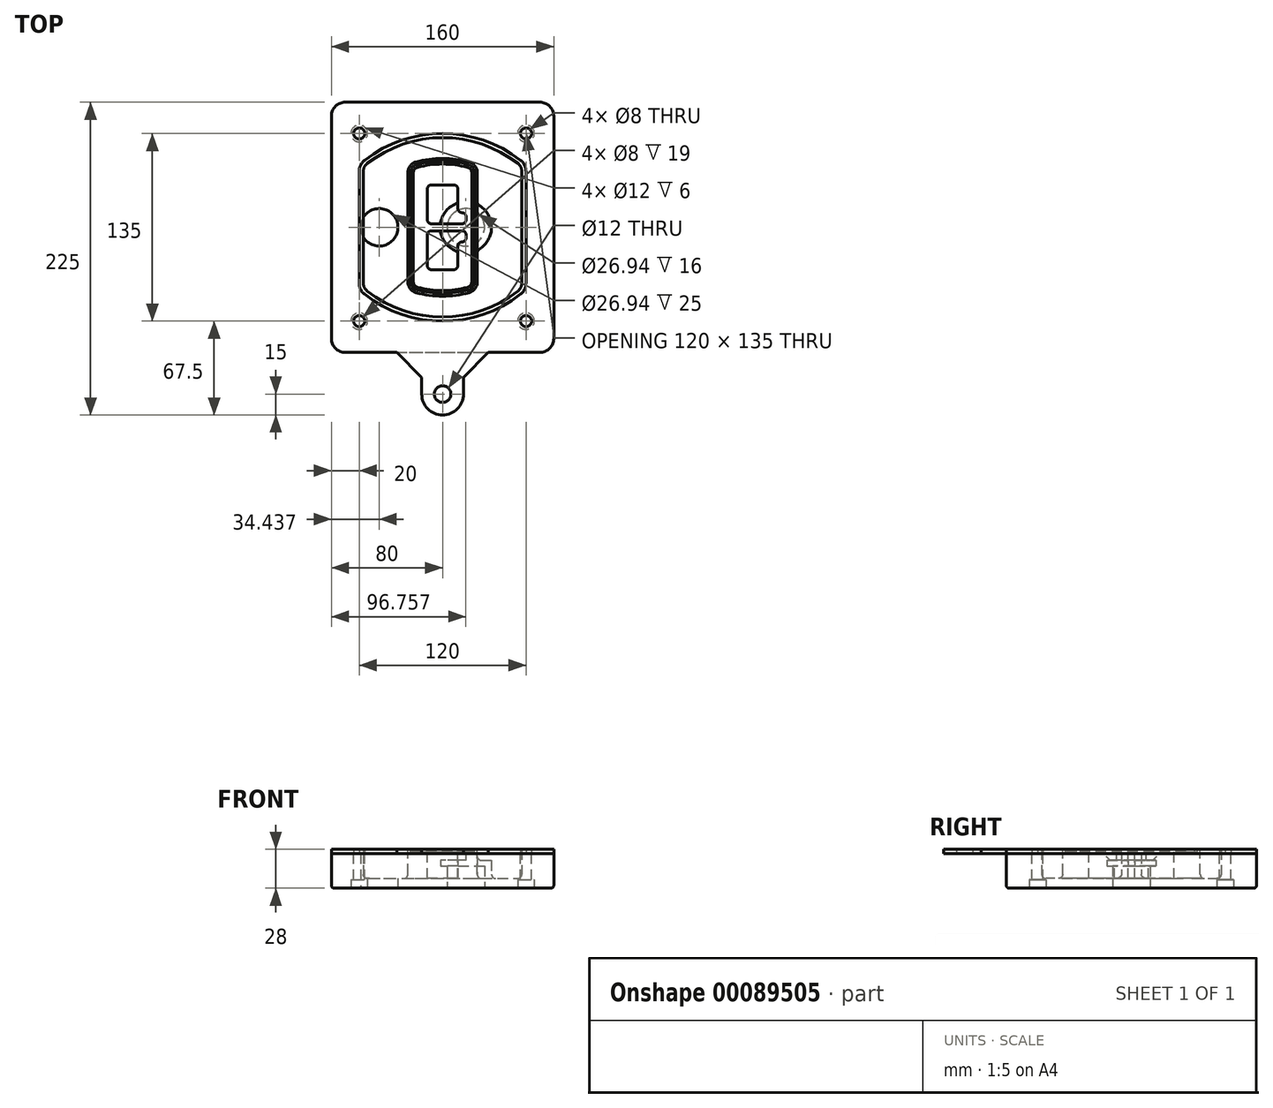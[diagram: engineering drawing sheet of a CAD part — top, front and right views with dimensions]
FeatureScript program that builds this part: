
annotation { "Feature Type Name" : "Feature", "Feature Type Description" : "" }
export const myFeature = defineFeature(function(context is Context, id is Id, definition is map)
    precondition{}
    {
        {
            var Q0;
            Q0=qCreatedBy(makeId("Top.planeOp"),FACE);
            var sketch = newSketch(context, id + "F0", { "sketchPlane" : qUnion([Q0])});
            skPoint(sketch, "E0.rect.middle", {"position": v(0, 0) * mm});
            skLineSegment(sketch, "E1.bottom", {"start": v(-70, -90) * mm, "end": v(70, -90) * mm});
            skLineSegment(sketch, "E1.top", {"start": v(-70, 90) * mm, "end": v(70, 90) * mm});
            skLineSegment(sketch, "E1.left", {"start": v(-80, -80) * mm, "end": v(-80, 80) * mm});
            skLineSegment(sketch, "E1.right", {"start": v(80, -80) * mm, "end": v(80, 80) * mm});
            skLineSegment(sketch, "E2", {"start": v(-80, 90) * mm, "end": v(80, -90) * mm, "construction": true});
            skLineSegment(sketch, "E3", {"start": v(80, 90) * mm, "end": v(-80, -90) * mm, "construction": true});
            skCircle(sketch, "E4", {"center": v(-60, 67.5) * mm, "radius": 4 * mm});
            skCircle(sketch, "E5", {"center": v(60, 67.5) * mm, "radius": 4 * mm});
            skCircle(sketch, "E6", {"center": v(60, -67.5) * mm, "radius": 4 * mm});
            skCircle(sketch, "E7", {"center": v(-60, -67.5) * mm, "radius": 4 * mm});
            skLineSegment(sketch, "E8", {"start": v(-60, 67.5) * mm, "end": v(60, 67.5) * mm, "construction": true});
            skLineSegment(sketch, "E9", {"start": v(60, 67.5) * mm, "end": v(60, -67.5) * mm, "construction": true});
            skLineSegment(sketch, "E10", {"start": v(60, -67.5) * mm, "end": v(-60, -67.5) * mm, "construction": true});
            skLineSegment(sketch, "E11", {"start": v(-60, -67.5) * mm, "end": v(-60, 67.5) * mm, "construction": true});
            skLineSegment(sketch, "E12", {"start": v(-60, 40.3) * mm, "end": v(-60, -40.3) * mm});
            skLineSegment(sketch, "E13", {"start": v(60, 40.3) * mm, "end": v(60, -40.3) * mm});
            skArc(sketch, "E14", {"start": v(56.15, 48.18) * mm, "mid": v(0, 67.5) * mm, "end": v(-56.15, 48.18) * mm});
            skArc(sketch, "E15", {"start": v(-56.15, -48.18) * mm, "mid": v(0, -67.5) * mm, "end": v(56.15, -48.18) * mm});
            skLineSegment(sketch, "E16", {"start": v(-60, 0) * mm, "end": v(60, 0) * mm, "construction": true});
            skPoint(sketch, "E17.visualSharp", {"position": v(-60, -45) * mm});
            skArc(sketch, "E17.filletArc", {"start": v(-60, -40.3) * mm, "mid": v(-58.99, -44.68) * mm, "end": v(-56.15, -48.18) * mm});
            skPoint(sketch, "E18.visualSharp", {"position": v(-60, 45) * mm});
            skArc(sketch, "E18.filletArc", {"start": v(-56.15, 48.18) * mm, "mid": v(-58.99, 44.68) * mm, "end": v(-60, 40.3) * mm});
            skPoint(sketch, "E19.visualSharp", {"position": v(60, 45) * mm});
            skArc(sketch, "E19.filletArc", {"start": v(60, 40.3) * mm, "mid": v(58.99, 44.68) * mm, "end": v(56.15, 48.18) * mm});
            skPoint(sketch, "E20.visualSharp", {"position": v(60, -45) * mm});
            skArc(sketch, "E20.filletArc", {"start": v(56.15, -48.18) * mm, "mid": v(58.99, -44.68) * mm, "end": v(60, -40.3) * mm});
            skPoint(sketch, "E21.visualSharp", {"position": v(-80, 90) * mm});
            skArc(sketch, "E21.filletArc", {"start": v(-70, 90) * mm, "mid": v(-77.07, 87.07) * mm, "end": v(-80, 80) * mm});
            skPoint(sketch, "E22.visualSharp", {"position": v(80, 90) * mm});
            skArc(sketch, "E22.filletArc", {"start": v(80, 80) * mm, "mid": v(77.07, 87.07) * mm, "end": v(70, 90) * mm});
            skPoint(sketch, "E23.visualSharp", {"position": v(80, -90) * mm});
            skArc(sketch, "E23.filletArc", {"start": v(70, -90) * mm, "mid": v(77.07, -87.07) * mm, "end": v(80, -80) * mm});
            skPoint(sketch, "E24.visualSharp", {"position": v(-80, -90) * mm});
            skArc(sketch, "E24.filletArc", {"start": v(-80, -80) * mm, "mid": v(-77.07, -87.07) * mm, "end": v(-70, -90) * mm});
            skArc(sketch, "E25.0", {"start": v(57, 40.3) * mm, "mid": v(56.3, 43.36) * mm, "end": v(54.3, 45.81) * mm});
            skLineSegment(sketch, "E25.1", {"start": v(57, 40.3) * mm, "end": v(57, -40.3) * mm});
            skArc(sketch, "E25.2", {"start": v(54.3, -45.81) * mm, "mid": v(56.3, -43.36) * mm, "end": v(57, -40.3) * mm});
            skArc(sketch, "E25.3", {"start": v(-54.3, -45.81) * mm, "mid": v(0, -64.5) * mm, "end": v(54.3, -45.81) * mm});
            skArc(sketch, "E25.4", {"start": v(-57, -40.3) * mm, "mid": v(-56.3, -43.36) * mm, "end": v(-54.3, -45.81) * mm});
            skArc(sketch, "E25.5", {"start": v(54.3, 45.81) * mm, "mid": v(0, 64.5) * mm, "end": v(-54.3, 45.81) * mm});
            skLineSegment(sketch, "E25.6", {"start": v(-57, 40.3) * mm, "end": v(-57, -40.3) * mm});
            skArc(sketch, "E25.7", {"start": v(-54.3, 45.81) * mm, "mid": v(-56.3, 43.36) * mm, "end": v(-57, 40.3) * mm});
            skArc(sketch, "E26.0", {"start": v(-58.62, 51.33) * mm, "mid": v(-62.58, 46.43) * mm, "end": v(-64, 40.3) * mm});
            skArc(sketch, "E26.1", {"start": v(58.62, 51.33) * mm, "mid": v(0, 71.5) * mm, "end": v(-58.62, 51.33) * mm});
            skArc(sketch, "E26.2", {"start": v(64, 40.3) * mm, "mid": v(62.58, 46.43) * mm, "end": v(58.62, 51.33) * mm});
            skLineSegment(sketch, "E26.3", {"start": v(64, 40.3) * mm, "end": v(64, -40.3) * mm});
            skArc(sketch, "E26.4", {"start": v(58.62, -51.33) * mm, "mid": v(62.58, -46.43) * mm, "end": v(64, -40.3) * mm});
            skLineSegment(sketch, "E26.5", {"start": v(-64, 40.3) * mm, "end": v(-64, -40.3) * mm});
            skArc(sketch, "E26.6", {"start": v(-58.62, -51.33) * mm, "mid": v(0, -71.5) * mm, "end": v(58.62, -51.33) * mm});
            skArc(sketch, "E26.7", {"start": v(-64, -40.3) * mm, "mid": v(-62.58, -46.43) * mm, "end": v(-58.62, -51.33) * mm});
            skSolve(sketch);
        }
        {
            var Q0;
            Q0=makeQuery(id+"F0.imprint","IMPRINT",FACE,{"disambiguationData":[TD([[makeQuery(id+"F0.imprint","IMPRINT",EDGE,{"derivedFrom":sQuery(id+"F0.wireOp",EDGE,"E1.bottom")}),1.0]])]});
            var Q1;
            Q1=makeQuery(id+"F0.imprint","IMPRINT",FACE,{"disambiguationData":[TD([[makeQuery(id+"F0.imprint","IMPRINT",EDGE,{"derivedFrom":sQuery(id+"F0.wireOp",EDGE,"E12")}),1.0]])]});
            var Q2;
            Q2=makeQuery(id+"F0.imprint","IMPRINT",FACE,{"disambiguationData":[TD([[makeQuery(id+"F0.imprint","IMPRINT",EDGE,{"derivedFrom":sQuery(id+"F0.wireOp",EDGE,"E25.0")}),1.0]])]});
            var Q3;
            Q3=makeQuery(id+"F0.imprint","IMPRINT",FACE,{"disambiguationData":[TD([[makeQuery(id+"F0.imprint","IMPRINT",EDGE,{"derivedFrom":sQuery(id+"F0.wireOp",EDGE,"E12")}),-1.0]])]});
            extrude(context, id + "F1", {"entities" : qUnion([Q0, Q1, Q2, Q3]), "oppositeDirection" : true, "depth" : 25 * mm});
        }
        {
            var Q0;
            Q0=makeQuery(id+"F0.imprint","IMPRINT",FACE,{"disambiguationData":[TD([[makeQuery(id+"F0.imprint","IMPRINT",EDGE,{"derivedFrom":sQuery(id+"F0.wireOp",EDGE,"E12")}),1.0]])]});
            extrude(context, id + "F2", {"entities" : qUnion([Q0]), "operationType" : NewBodyOperationType.ADD, "depth" : 3 * mm});
        }
        {
            var Q0;
            Q0=makeQuery(id+"F0.imprint","IMPRINT",FACE,{"disambiguationData":[TD([[makeQuery(id+"F0.imprint","IMPRINT",EDGE,{"derivedFrom":sQuery(id+"F0.wireOp",EDGE,"E25.0")}),1.0]])]});
            extrude(context, id + "F3", {"entities" : qUnion([Q0]), "operationType" : NewBodyOperationType.REMOVE, "oppositeDirection" : true, "depth" : 18 * mm});
        }
        {
            var Q0;
            Q0=makeQuery(id+"F2.opExtrude","CAP_FACE",FACE,{"disambiguationData":[OSD([sQuery(id+"F0.wireOp",EDGE,"E12"),sQuery(id+"F0.wireOp",EDGE,"E13"),sQuery(id+"F0.wireOp",EDGE,"E14"),sQuery(id+"F0.wireOp",EDGE,"E15"),sQuery(id+"F0.wireOp",EDGE,"E17.filletArc"),sQuery(id+"F0.wireOp",EDGE,"E18.filletArc"),sQuery(id+"F0.wireOp",EDGE,"E19.filletArc"),sQuery(id+"F0.wireOp",EDGE,"E20.filletArc"),sQuery(id+"F0.wireOp",EDGE,"E25.0"),sQuery(id+"F0.wireOp",EDGE,"E25.1"),sQuery(id+"F0.wireOp",EDGE,"E25.2"),sQuery(id+"F0.wireOp",EDGE,"E25.3"),sQuery(id+"F0.wireOp",EDGE,"E25.4"),sQuery(id+"F0.wireOp",EDGE,"E25.5"),sQuery(id+"F0.wireOp",EDGE,"E25.6"),sQuery(id+"F0.wireOp",EDGE,"E25.7")])],"isStart":false});
            var sketch = newSketch(context, id + "F4", { "sketchPlane" : qUnion([Q0])});
            skArc(sketch, "E27.0", {"start": v(-19.08, -46.97) * mm, "mid": v(0, -49.5) * mm, "end": v(19.08, -46.97) * mm});
            skArc(sketch, "E28.0", {"start": v(19.08, 46.97) * mm, "mid": v(0, 49.5) * mm, "end": v(-19.08, 46.97) * mm});
            skLineSegment(sketch, "E29", {"start": v(-25, 39.25) * mm, "end": v(-25, -39.25) * mm});
            skLineSegment(sketch, "E30", {"start": v(25, 39.25) * mm, "end": v(25, -39.25) * mm});
            skLineSegment(sketch, "E31", {"start": v(-25, 45.1) * mm, "end": v(25, 45.1) * mm, "construction": true});
            skLineSegment(sketch, "E32", {"start": v(-25, -45.1) * mm, "end": v(25, -45.1) * mm, "construction": true});
            skPoint(sketch, "E33.visualSharp", {"position": v(-25, 45.1) * mm});
            skArc(sketch, "E33.filletArc", {"start": v(-19.08, 46.97) * mm, "mid": v(-23.35, 44.11) * mm, "end": v(-25, 39.25) * mm});
            skPoint(sketch, "E34.visualSharp", {"position": v(25, 45.1) * mm});
            skArc(sketch, "E34.filletArc", {"start": v(25, 39.25) * mm, "mid": v(23.35, 44.11) * mm, "end": v(19.08, 46.97) * mm});
            skPoint(sketch, "E35.visualSharp", {"position": v(25, -45.1) * mm});
            skArc(sketch, "E35.filletArc", {"start": v(19.08, -46.97) * mm, "mid": v(23.35, -44.11) * mm, "end": v(25, -39.25) * mm});
            skPoint(sketch, "E36.visualSharp", {"position": v(-25, -45.1) * mm});
            skArc(sketch, "E36.filletArc", {"start": v(-25, -39.25) * mm, "mid": v(-23.35, -44.11) * mm, "end": v(-19.08, -46.97) * mm});
            skArc(sketch, "E37.0", {"start": v(54.3, 45.81) * mm, "mid": v(0, 64.5) * mm, "end": v(-54.3, 45.81) * mm});
            skArc(sketch, "E37.1", {"start": v(-54.3, 45.81) * mm, "mid": v(-56.3, 43.36) * mm, "end": v(-57, 40.3) * mm});
            skLineSegment(sketch, "E37.2", {"start": v(-57, 40.3) * mm, "end": v(-57, -40.3) * mm});
            skArc(sketch, "E37.3", {"start": v(-57, -40.3) * mm, "mid": v(-56.3, -43.36) * mm, "end": v(-54.3, -45.81) * mm});
            skArc(sketch, "E37.4", {"start": v(-54.3, -45.81) * mm, "mid": v(0, -64.5) * mm, "end": v(54.3, -45.81) * mm});
            skArc(sketch, "E37.5", {"start": v(54.3, -45.81) * mm, "mid": v(56.3, -43.36) * mm, "end": v(57, -40.3) * mm});
            skLineSegment(sketch, "E37.6", {"start": v(57, 40.3) * mm, "end": v(57, -40.3) * mm});
            skArc(sketch, "E37.7", {"start": v(57, 40.3) * mm, "mid": v(56.3, 43.36) * mm, "end": v(54.3, 45.81) * mm});
            skLineSegment(sketch, "E38.0", {"start": v(23, 39.25) * mm, "end": v(23, -39.25) * mm});
            skArc(sketch, "E38.1", {"start": v(18.56, -45.04) * mm, "mid": v(21.76, -42.9) * mm, "end": v(23, -39.25) * mm});
            skArc(sketch, "E38.2", {"start": v(-18.56, -45.04) * mm, "mid": v(0, -47.5) * mm, "end": v(18.56, -45.04) * mm});
            skArc(sketch, "E38.3", {"start": v(-23, -39.25) * mm, "mid": v(-21.76, -42.9) * mm, "end": v(-18.56, -45.04) * mm});
            skLineSegment(sketch, "E38.4", {"start": v(-23, 39.25) * mm, "end": v(-23, -39.25) * mm});
            skArc(sketch, "E38.5", {"start": v(23, 39.25) * mm, "mid": v(21.76, 42.9) * mm, "end": v(18.56, 45.04) * mm});
            skArc(sketch, "E38.6", {"start": v(-18.56, 45.04) * mm, "mid": v(-21.76, 42.9) * mm, "end": v(-23, 39.25) * mm});
            skArc(sketch, "E38.7", {"start": v(18.56, 45.04) * mm, "mid": v(0, 47.5) * mm, "end": v(-18.56, 45.04) * mm});
            skArc(sketch, "E39.0", {"start": v(21, 39.25) * mm, "mid": v(20.18, 41.68) * mm, "end": v(18.04, 43.1) * mm});
            skLineSegment(sketch, "E39.1", {"start": v(21, 39.25) * mm, "end": v(21, -39.25) * mm});
            skArc(sketch, "E39.2", {"start": v(18.04, -43.1) * mm, "mid": v(20.18, -41.68) * mm, "end": v(21, -39.25) * mm});
            skArc(sketch, "E39.3", {"start": v(-18.04, -43.1) * mm, "mid": v(0, -45.5) * mm, "end": v(18.04, -43.1) * mm});
            skArc(sketch, "E39.4", {"start": v(-21, -39.25) * mm, "mid": v(-20.18, -41.68) * mm, "end": v(-18.04, -43.1) * mm});
            skArc(sketch, "E39.5", {"start": v(18.04, 43.1) * mm, "mid": v(0, 45.5) * mm, "end": v(-18.04, 43.1) * mm});
            skLineSegment(sketch, "E39.6", {"start": v(-21, 39.25) * mm, "end": v(-21, -39.25) * mm});
            skArc(sketch, "E39.7", {"start": v(-18.04, 43.1) * mm, "mid": v(-20.18, 41.68) * mm, "end": v(-21, 39.25) * mm});
            skLineSegment(sketch, "E40", {"start": v(-25, 0) * mm, "end": v(25, 0) * mm, "construction": true});
            skLineSegment(sketch, "E41", {"start": v(-11, 5.5) * mm, "end": v(-11, 27.5) * mm});
            skLineSegment(sketch, "E42", {"start": v(-8, 30.5) * mm, "end": v(8, 30.5) * mm});
            skLineSegment(sketch, "E43", {"start": v(11, 27.5) * mm, "end": v(11, 13.5) * mm});
            skLineSegment(sketch, "E44", {"start": v(14, 10.5) * mm, "end": v(14, 10.5) * mm});
            skLineSegment(sketch, "E45", {"start": v(17, 7.5) * mm, "end": v(17, 5.5) * mm});
            skLineSegment(sketch, "E46", {"start": v(14, 2.5) * mm, "end": v(-8, 2.5) * mm});
            skPoint(sketch, "E47.visualSharp", {"position": v(-11, 30.5) * mm});
            skArc(sketch, "E47.filletArc", {"start": v(-8, 30.5) * mm, "mid": v(-10.12, 29.62) * mm, "end": v(-11, 27.5) * mm});
            skPoint(sketch, "E48.visualSharp", {"position": v(11, 30.5) * mm});
            skArc(sketch, "E48.filletArc", {"start": v(11, 27.5) * mm, "mid": v(10.12, 29.62) * mm, "end": v(8, 30.5) * mm});
            skPoint(sketch, "E49.visualSharp", {"position": v(11, 10.5) * mm});
            skArc(sketch, "E49.filletArc", {"start": v(11, 13.5) * mm, "mid": v(11.88, 11.38) * mm, "end": v(14, 10.5) * mm});
            skPoint(sketch, "E50.visualSharp", {"position": v(17, 10.5) * mm});
            skArc(sketch, "E50.filletArc", {"start": v(17, 7.5) * mm, "mid": v(16.12, 9.62) * mm, "end": v(14, 10.5) * mm});
            skPoint(sketch, "E51.visualSharp", {"position": v(17, 2.5) * mm});
            skArc(sketch, "E51.filletArc", {"start": v(14, 2.5) * mm, "mid": v(16.12, 3.38) * mm, "end": v(17, 5.5) * mm});
            skPoint(sketch, "E52.visualSharp", {"position": v(-11, 2.5) * mm});
            skArc(sketch, "E52.filletArc", {"start": v(-11, 5.5) * mm, "mid": v(-10.12, 3.38) * mm, "end": v(-8, 2.5) * mm});
            skLineSegment(sketch, "E53.0.MirrorCS", {"start": v(14, -2.5) * mm, "end": v(-8, -2.5) * mm});
            skArc(sketch, "E54.0.MirrorCS", {"start": v(-11, -5.5) * mm, "mid": v(-10.12, -3.38) * mm, "end": v(-8, -2.5) * mm});
            skLineSegment(sketch, "E55.0.MirrorCS", {"start": v(-11, -5.5) * mm, "end": v(-11, -27.5) * mm});
            skArc(sketch, "E56.0.MirrorCS", {"start": v(-8, -30.5) * mm, "mid": v(-10.12, -29.62) * mm, "end": v(-11, -27.5) * mm});
            skLineSegment(sketch, "E57.0.MirrorCS", {"start": v(-8, -30.5) * mm, "end": v(8, -30.5) * mm});
            skArc(sketch, "E58.0.MirrorCS", {"start": v(11, -27.5) * mm, "mid": v(10.12, -29.62) * mm, "end": v(8, -30.5) * mm});
            skLineSegment(sketch, "E59.0.MirrorCS", {"start": v(11, -27.5) * mm, "end": v(11, -13.5) * mm});
            skArc(sketch, "E60.0.MirrorCS", {"start": v(11, -13.5) * mm, "mid": v(11.88, -11.38) * mm, "end": v(14, -10.5) * mm});
            skArc(sketch, "E61.0.MirrorCS", {"start": v(17, -7.5) * mm, "mid": v(16.12, -9.62) * mm, "end": v(14, -10.5) * mm});
            skLineSegment(sketch, "E62.0.MirrorCS", {"start": v(17, -7.5) * mm, "end": v(17, -5.5) * mm});
            skArc(sketch, "E63.0.MirrorCS", {"start": v(14, -2.5) * mm, "mid": v(16.12, -3.38) * mm, "end": v(17, -5.5) * mm});
            skSolve(sketch);
        }
        {
            var Q0;
            Q0=makeQuery(id+"F4.imprint","IMPRINT",FACE,{"disambiguationData":[TD([[makeQuery(id+"F4.imprint","IMPRINT",EDGE,{"derivedFrom":sQuery(id+"F4.wireOp",EDGE,"E27.0")}),1.0]])]});
            var Q1;
            Q1=makeQuery(id+"F4.imprint","IMPRINT",FACE,{"disambiguationData":[TD([[makeQuery(id+"F4.imprint","IMPRINT",EDGE,{"derivedFrom":sQuery(id+"F4.wireOp",EDGE,"E38.0")}),-1.0]])]});
            var Q2;
            Q2=makeQuery(id+"F4.imprint","IMPRINT",FACE,{"disambiguationData":[TD([[makeQuery(id+"F4.imprint","IMPRINT",EDGE,{"derivedFrom":sQuery(id+"F4.wireOp",EDGE,"E39.0")}),1.0]])]});
            extrude(context, id + "F5", {"entities" : qUnion([Q0, Q1, Q2]), "operationType" : NewBodyOperationType.ADD, "endBound" : BoundingType.UP_TO_NEXT, "oppositeDirection" : true, "depth" : 25 * mm});
        }
        {
            var Q0;
            Q0=makeQuery(id+"F4.imprint","IMPRINT",FACE,{"disambiguationData":[TD([[makeQuery(id+"F4.imprint","IMPRINT",EDGE,{"derivedFrom":sQuery(id+"F4.wireOp",EDGE,"E38.0")}),-1.0]])]});
            extrude(context, id + "F6", {"entities" : qUnion([Q0]), "operationType" : NewBodyOperationType.REMOVE, "oppositeDirection" : true, "depth" : 2 * mm});
        }
        {
            var Q0;
            Q0=makeQuery(id+"F1.opExtrude","CAP_FACE",FACE,{"disambiguationData":[OSD([sQuery(id+"F0.wireOp",EDGE,"E1.bottom"),sQuery(id+"F0.wireOp",EDGE,"E1.top"),sQuery(id+"F0.wireOp",EDGE,"E1.left"),sQuery(id+"F0.wireOp",EDGE,"E1.right"),sQuery(id+"F0.wireOp",EDGE,"E4"),sQuery(id+"F0.wireOp",EDGE,"E5"),sQuery(id+"F0.wireOp",EDGE,"E6"),sQuery(id+"F0.wireOp",EDGE,"E7"),sQuery(id+"F0.wireOp",EDGE,"E21.filletArc"),sQuery(id+"F0.wireOp",EDGE,"E22.filletArc"),sQuery(id+"F0.wireOp",EDGE,"E23.filletArc"),sQuery(id+"F0.wireOp",EDGE,"E24.filletArc")])],"isStart":false});
            var sketch = newSketch(context, id + "F7", { "sketchPlane" : qUnion([Q0])});
            skCircle(sketch, "E64", {"center": v(16.76, 0) * mm, "radius": 13.47 * mm});
            skCircle(sketch, "E65", {"center": v(-45.56, 0) * mm, "radius": 13.47 * mm});
            skLineSegment(sketch, "E66", {"start": v(80, 0) * mm, "end": v(-80, 0) * mm});
            skCircle(sketch, "E67", {"center": v(16.76, 0) * mm, "radius": 18.47 * mm});
            skCircle(sketch, "E68", {"center": v(60, -67.5) * mm, "radius": 6 * mm});
            skCircle(sketch, "E69", {"center": v(-60, -67.5) * mm, "radius": 6 * mm});
            skCircle(sketch, "E70", {"center": v(-60, 67.5) * mm, "radius": 6 * mm});
            skCircle(sketch, "E71", {"center": v(60, 67.5) * mm, "radius": 6 * mm});
            skSolve(sketch);
        }
        {
            var Q0;
            {var subQ1=sQuery(id+"F7.wireOp",EDGE,"E66");var subQ4=sQuery(id+"F7.wireOp",EDGE,"E64");var subQ6=makeQuery(id+"F7.imprint","INTERSECT",VERTEX,{"disambiguationData":[OD(0.0)],"derivedFrom":[subQ4,subQ1]});Q0=makeQuery(id+"F7.imprint","IMPRINT",FACE,{"disambiguationData":[TD([[makeQuery(id+"F7.imprint","IMPRINT",EDGE,{"disambiguationData":[TD([[subQ6,-1.0]])],"derivedFrom":subQ4}),-1.0]])]});}
            var Q1;
            {var subQ0=sQuery(id+"F7.wireOp",EDGE,"E66");var subQ1=sQuery(id+"F7.wireOp",EDGE,"E64");var subQ3=makeQuery(id+"F7.imprint","INTERSECT",VERTEX,{"disambiguationData":[OD(0.0)],"derivedFrom":[subQ1,subQ0]});Q1=makeQuery(id+"F7.imprint","IMPRINT",FACE,{"disambiguationData":[TD([[makeQuery(id+"F7.imprint","IMPRINT",EDGE,{"disambiguationData":[TD([[subQ3,-1.0]])],"derivedFrom":subQ1}),1.0]])]});}
            var Q2;
            {var subQ0=sQuery(id+"F7.wireOp",EDGE,"E66");var subQ1=sQuery(id+"F7.wireOp",EDGE,"E64");var subQ3=makeQuery(id+"F7.imprint","INTERSECT",VERTEX,{"disambiguationData":[OD(0.0)],"derivedFrom":[subQ1,subQ0]});Q2=makeQuery(id+"F7.imprint","IMPRINT",FACE,{"disambiguationData":[TD([[makeQuery(id+"F7.imprint","IMPRINT",EDGE,{"disambiguationData":[TD([[subQ3,1.0]])],"derivedFrom":subQ1}),1.0]])]});}
            var Q3;
            {var subQ1=sQuery(id+"F7.wireOp",EDGE,"E66");var subQ4=sQuery(id+"F7.wireOp",EDGE,"E64");var subQ6=makeQuery(id+"F7.imprint","INTERSECT",VERTEX,{"disambiguationData":[OD(0.0)],"derivedFrom":[subQ4,subQ1]});Q3=makeQuery(id+"F7.imprint","IMPRINT",FACE,{"disambiguationData":[TD([[makeQuery(id+"F7.imprint","IMPRINT",EDGE,{"disambiguationData":[TD([[subQ6,1.0]])],"derivedFrom":subQ4}),-1.0]])]});}
            extrude(context, id + "F8", {"entities" : qUnion([Q0, Q1, Q2, Q3]), "operationType" : NewBodyOperationType.ADD, "oppositeDirection" : true, "depth" : 20 * mm});
        }
        {
            var Q0;
            {var subQ0=sQuery(id+"F7.wireOp",EDGE,"E66");var subQ1=sQuery(id+"F7.wireOp",EDGE,"E64");var subQ3=makeQuery(id+"F7.imprint","INTERSECT",VERTEX,{"disambiguationData":[OD(0.0)],"derivedFrom":[subQ1,subQ0]});Q0=makeQuery(id+"F7.imprint","IMPRINT",FACE,{"disambiguationData":[TD([[makeQuery(id+"F7.imprint","IMPRINT",EDGE,{"disambiguationData":[TD([[subQ3,-1.0]])],"derivedFrom":subQ1}),1.0]])]});}
            var Q1;
            {var subQ0=sQuery(id+"F7.wireOp",EDGE,"E66");var subQ1=sQuery(id+"F7.wireOp",EDGE,"E64");var subQ3=makeQuery(id+"F7.imprint","INTERSECT",VERTEX,{"disambiguationData":[OD(0.0)],"derivedFrom":[subQ1,subQ0]});Q1=makeQuery(id+"F7.imprint","IMPRINT",FACE,{"disambiguationData":[TD([[makeQuery(id+"F7.imprint","IMPRINT",EDGE,{"disambiguationData":[TD([[subQ3,1.0]])],"derivedFrom":subQ1}),1.0]])]});}
            extrude(context, id + "F9", {"entities" : qUnion([Q0, Q1]), "operationType" : NewBodyOperationType.REMOVE, "oppositeDirection" : true, "depth" : 16 * mm});
        }
        {
            var Q0;
            {var subQ0=sQuery(id+"F7.wireOp",EDGE,"E66");var subQ1=sQuery(id+"F7.wireOp",EDGE,"E65");var subQ3=makeQuery(id+"F7.imprint","INTERSECT",VERTEX,{"disambiguationData":[OD(0.0)],"derivedFrom":[subQ1,subQ0]});Q0=makeQuery(id+"F7.imprint","IMPRINT",FACE,{"disambiguationData":[TD([[makeQuery(id+"F7.imprint","IMPRINT",EDGE,{"disambiguationData":[TD([[subQ3,-1.0]])],"derivedFrom":subQ1}),1.0]])]});}
            var Q1;
            {var subQ0=sQuery(id+"F7.wireOp",EDGE,"E66");var subQ1=sQuery(id+"F7.wireOp",EDGE,"E65");var subQ3=makeQuery(id+"F7.imprint","INTERSECT",VERTEX,{"disambiguationData":[OD(0.0)],"derivedFrom":[subQ1,subQ0]});Q1=makeQuery(id+"F7.imprint","IMPRINT",FACE,{"disambiguationData":[TD([[makeQuery(id+"F7.imprint","IMPRINT",EDGE,{"disambiguationData":[TD([[subQ3,1.0]])],"derivedFrom":subQ1}),1.0]])]});}
            extrude(context, id + "F10", {"entities" : qUnion([Q0, Q1]), "operationType" : NewBodyOperationType.REMOVE, "oppositeDirection" : true, "depth" : 25 * mm});
        }
        {
            var Q0;
            Q0=makeQuery(id+"F7.imprint","IMPRINT",FACE,{"disambiguationData":[TD([[makeQuery(id+"F7.imprint","IMPRINT",EDGE,{"derivedFrom":sQuery(id+"F7.wireOp",EDGE,"E68")}),1.0]])]});
            var Q1;
            Q1=makeQuery(id+"F7.imprint","IMPRINT",FACE,{"disambiguationData":[TD([[makeQuery(id+"F7.imprint","IMPRINT",EDGE,{"derivedFrom":makeQuery(id+"F1.opExtrude","CAP_EDGE",EDGE,{"disambiguationData":[OSD([sQuery(id+"F0.wireOp",EDGE,"E5")])],"isStart":false})}),-1.0]])]});
            var Q2;
            Q2=makeQuery(id+"F7.imprint","IMPRINT",FACE,{"disambiguationData":[TD([[makeQuery(id+"F7.imprint","IMPRINT",EDGE,{"derivedFrom":sQuery(id+"F7.wireOp",EDGE,"E69")}),1.0]])]});
            var Q3;
            Q3=makeQuery(id+"F7.imprint","IMPRINT",FACE,{"disambiguationData":[TD([[makeQuery(id+"F7.imprint","IMPRINT",EDGE,{"derivedFrom":makeQuery(id+"F1.opExtrude","CAP_EDGE",EDGE,{"disambiguationData":[OSD([sQuery(id+"F0.wireOp",EDGE,"E4")])],"isStart":false})}),-1.0]])]});
            var Q4;
            Q4=makeQuery(id+"F7.imprint","IMPRINT",FACE,{"disambiguationData":[TD([[makeQuery(id+"F7.imprint","IMPRINT",EDGE,{"derivedFrom":sQuery(id+"F7.wireOp",EDGE,"E70")}),1.0]])]});
            var Q5;
            Q5=makeQuery(id+"F7.imprint","IMPRINT",FACE,{"disambiguationData":[TD([[makeQuery(id+"F7.imprint","IMPRINT",EDGE,{"derivedFrom":makeQuery(id+"F1.opExtrude","CAP_EDGE",EDGE,{"disambiguationData":[OSD([sQuery(id+"F0.wireOp",EDGE,"E7")])],"isStart":false})}),-1.0]])]});
            var Q6;
            Q6=makeQuery(id+"F7.imprint","IMPRINT",FACE,{"disambiguationData":[TD([[makeQuery(id+"F7.imprint","IMPRINT",EDGE,{"derivedFrom":sQuery(id+"F7.wireOp",EDGE,"E71")}),1.0]])]});
            var Q7;
            Q7=makeQuery(id+"F7.imprint","IMPRINT",FACE,{"disambiguationData":[TD([[makeQuery(id+"F7.imprint","IMPRINT",EDGE,{"derivedFrom":makeQuery(id+"F1.opExtrude","CAP_EDGE",EDGE,{"disambiguationData":[OSD([sQuery(id+"F0.wireOp",EDGE,"E6")])],"isStart":false})}),-1.0]])]});
            extrude(context, id + "F11", {"entities" : qUnion([Q0, Q1, Q2, Q3, Q4, Q5, Q6, Q7]), "operationType" : NewBodyOperationType.REMOVE, "oppositeDirection" : true, "depth" : 6 * mm});
        }
        {
            var Q0;
            Q0=makeQuery(id+"F9.boolean.opBoolean","COPY",FACE,{"derivedFrom":makeQuery(id+"F9.opExtrude","CAP_FACE",FACE,{"disambiguationData":[OSD([sQuery(id+"F7.wireOp",EDGE,"E64")])],"isStart":false})});
            var sketch = newSketch(context, id + "F12", { "sketchPlane" : qUnion([Q0])});
            skArc(sketch, "E72.0", {"start": v(11, 17.55) * mm, "mid": v(2.57, 11.82) * mm, "end": v(-1.54, 2.5) * mm});
            skArc(sketch, "E72.1", {"start": v(-1.54, -2.5) * mm, "mid": v(2.57, -11.82) * mm, "end": v(11, -17.55) * mm});
            skLineSegment(sketch, "E73", {"start": v(-1.54, -2.5) * mm, "end": v(14, -2.5) * mm});
            skLineSegment(sketch, "E74.0", {"start": v(14, 2.5) * mm, "end": v(-1.54, 2.5) * mm});
            skArc(sketch, "E74.1", {"start": v(14, 2.5) * mm, "mid": v(16.12, 3.38) * mm, "end": v(17, 5.5) * mm});
            skLineSegment(sketch, "E74.2", {"start": v(17, 7.5) * mm, "end": v(17, 5.5) * mm});
            skArc(sketch, "E74.3", {"start": v(17, 7.5) * mm, "mid": v(16.12, 9.62) * mm, "end": v(14, 10.5) * mm});
            skArc(sketch, "E74.4", {"start": v(11, 13.5) * mm, "mid": v(11.88, 11.38) * mm, "end": v(14, 10.5) * mm});
            skLineSegment(sketch, "E74.5", {"start": v(11, 17.55) * mm, "end": v(11, 13.5) * mm});
            skLineSegment(sketch, "E74.7", {"start": v(14, -2.5) * mm, "end": v(-1.54, -2.5) * mm});
            skArc(sketch, "E74.8", {"start": v(14, -2.5) * mm, "mid": v(16.12, -3.38) * mm, "end": v(17, -5.5) * mm});
            skLineSegment(sketch, "E74.9", {"start": v(17, -7.5) * mm, "end": v(17, -5.5) * mm});
            skArc(sketch, "E74.10", {"start": v(17, -7.5) * mm, "mid": v(16.12, -9.62) * mm, "end": v(14, -10.5) * mm});
            skArc(sketch, "E74.11", {"start": v(11, -13.5) * mm, "mid": v(11.88, -11.38) * mm, "end": v(14, -10.5) * mm});
            skLineSegment(sketch, "E74.12", {"start": v(11, -17.55) * mm, "end": v(11, -13.5) * mm});
            skPoint(sketch, "E75.orphan", {"position": v(11, -27.5) * mm});
            skPoint(sketch, "E76.orphan", {"position": v(-8, -2.5) * mm});
            skPoint(sketch, "E77.orphan", {"position": v(-8, 2.5) * mm});
            skPoint(sketch, "E78.orphan", {"position": v(11, 27.5) * mm});
            skSolve(sketch);
        }
        {
            var Q0;
            {var subQ7=sQuery(id+"F12.wireOp",EDGE,"E72.0");var subQ14=sQuery(id+"F12.wireOp",EDGE,"E72.1");var subQ16=sQuery(id+"F12.wireOp",EDGE,"E74.1");var subQ18=sQuery(id+"F12.wireOp",EDGE,"E74.8");Q0=qUnion([makeQuery(id+"F12.imprint","IMPRINT",FACE,{"disambiguationData":[TD([[makeQuery(id+"F12.imprint","IMPRINT",EDGE,{"derivedFrom":subQ7}),1.0]])]}),makeQuery(id+"F12.imprint","IMPRINT",FACE,{"disambiguationData":[TD([[makeQuery(id+"F12.imprint","IMPRINT",EDGE,{"derivedFrom":subQ14}),1.0]])]}),makeQuery(id+"F12.imprint","IMPRINT",FACE,{"disambiguationData":[TD([[makeQuery(id+"F12.imprint","IMPRINT",EDGE,{"derivedFrom":subQ16}),1.0]])]}),makeQuery(id+"F12.imprint","IMPRINT",FACE,{"disambiguationData":[TD([[makeQuery(id+"F12.imprint","IMPRINT",EDGE,{"derivedFrom":subQ18}),-1.0]])]})]);}
            var Q1;
            Q1=makeQuery(id+"F5.boolean.opBoolean","SPLIT",FACE,{"disambiguationData":[TD([makeQuery(id+"F5.opExtrude","SWEPT_FACE",FACE,{"disambiguationData":[OSD([sQuery(id+"F4.wireOp",EDGE,"E41")])]})])],"derivedFrom":makeQuery(id+"F3.boolean.opBoolean","COPY",FACE,{"derivedFrom":makeQuery(id+"F3.opExtrude","CAP_FACE",FACE,{"disambiguationData":[OSD([sQuery(id+"F0.wireOp",EDGE,"E25.0"),sQuery(id+"F0.wireOp",EDGE,"E25.1"),sQuery(id+"F0.wireOp",EDGE,"E25.2"),sQuery(id+"F0.wireOp",EDGE,"E25.3"),sQuery(id+"F0.wireOp",EDGE,"E25.4"),sQuery(id+"F0.wireOp",EDGE,"E25.5"),sQuery(id+"F0.wireOp",EDGE,"E25.6"),sQuery(id+"F0.wireOp",EDGE,"E25.7")])],"isStart":false})})});
            extrude(context, id + "F13", {"entities" : qUnion([Q0]), "operationType" : NewBodyOperationType.REMOVE, "endBound" : BoundingType.UP_TO_SURFACE, "endBoundEntityFace" : qUnion([Q1]), "depth" : 25 * mm});
        }
        {
            var Q0;
            Q0=makeQuery(id+"F3.boolean.opBoolean","COPY",EDGE,{"derivedFrom":makeQuery(id+"F3.opExtrude","CAP_EDGE",EDGE,{"disambiguationData":[OSD([sQuery(id+"F0.wireOp",EDGE,"E25.6")])],"isStart":false})});
            var Q1;
            Q1=makeQuery(id+"F8.boolean.opBoolean","INTERSECT",EDGE,{"derivedFrom":[makeQuery(id+"F5.opExtrude","SWEPT_FACE",FACE,{"disambiguationData":[OSD([sQuery(id+"F4.wireOp",EDGE,"E30")])]}),makeQuery(id+"F8.opExtrude","CAP_FACE",FACE,{"disambiguationData":[OSD([sQuery(id+"F7.wireOp",EDGE,"E67")])],"isStart":false})]});
            var Q2;
            Q2=makeQuery(id+"F8.boolean.opBoolean","INTERSECT",EDGE,{"disambiguationData":[OD(1.0)],"derivedFrom":[makeQuery(id+"F5.opExtrude","SWEPT_FACE",FACE,{"disambiguationData":[OSD([sQuery(id+"F4.wireOp",EDGE,"E30")])]}),makeQuery(id+"F8.opExtrude","SWEPT_FACE",FACE,{"disambiguationData":[OSD([sQuery(id+"F7.wireOp",EDGE,"E67")])]})]});
            var Q3;
            {var subQ0=sQuery(id+"F4.wireOp",EDGE,"E30");Q3=makeQuery(id+"F8.boolean.opBoolean","SPLIT",EDGE,{"disambiguationData":[TD([makeQuery(id+"F5.opExtrude","SWEPT_FACE",FACE,{"disambiguationData":[OSD([sQuery(id+"F4.wireOp",EDGE,"E35.filletArc")])]})])],"derivedFrom":makeQuery(id+"F5.opExtrude","CAP_EDGE",EDGE,{"disambiguationData":[OSD([subQ0])],"isStart":false})});}
            var Q4;
            {var subQ0=sQuery(id+"F0.wireOp",EDGE,"E25.7");var subQ1=sQuery(id+"F0.wireOp",EDGE,"E25.1");var subQ2=sQuery(id+"F0.wireOp",EDGE,"E25.6");var subQ3=sQuery(id+"F0.wireOp",EDGE,"E25.5");var subQ4=sQuery(id+"F0.wireOp",EDGE,"E25.4");var subQ5=sQuery(id+"F0.wireOp",EDGE,"E25.0");var subQ6=sQuery(id+"F0.wireOp",EDGE,"E25.2");var subQ7=sQuery(id+"F0.wireOp",EDGE,"E25.3");Q4=makeQuery(id+"F8.boolean.opBoolean","INTERSECT",EDGE,{"derivedFrom":[makeQuery(id+"F5.boolean.opBoolean","SPLIT",FACE,{"disambiguationData":[TD([makeQuery(id+"F2.opExtrude","SWEPT_FACE",FACE,{"disambiguationData":[OSD([subQ5])]})])],"derivedFrom":makeQuery(id+"F3.boolean.opBoolean","COPY",FACE,{"derivedFrom":makeQuery(id+"F3.opExtrude","CAP_FACE",FACE,{"disambiguationData":[OSD([subQ5,subQ1,subQ6,subQ7,subQ4,subQ3,subQ2,subQ0])],"isStart":false})})}),makeQuery(id+"F8.opExtrude","SWEPT_FACE",FACE,{"disambiguationData":[OSD([sQuery(id+"F7.wireOp",EDGE,"E67")])]})]});}
            var Q5;
            Q5=makeQuery(id+"F8.boolean.opBoolean","INTERSECT",EDGE,{"disambiguationData":[OD(0.0)],"derivedFrom":[makeQuery(id+"F5.opExtrude","SWEPT_FACE",FACE,{"disambiguationData":[OSD([sQuery(id+"F4.wireOp",EDGE,"E30")])]}),makeQuery(id+"F8.opExtrude","SWEPT_FACE",FACE,{"disambiguationData":[OSD([sQuery(id+"F7.wireOp",EDGE,"E67")])]})]});
            fillet(context, id + "F14", {"entities" : qUnion([Q0, Q1, Q2, Q3, Q4, Q5]), "radius" : 3 * mm, "tangentPropagation" : true, "allowEdgeOverflow" : false});
        }
        {
            var Q0;
            Q0=makeQuery(id+"F1.opExtrude","CAP_EDGE",EDGE,{"disambiguationData":[OSD([sQuery(id+"F0.wireOp",EDGE,"E1.bottom")])],"isStart":false});
            fillet(context, id + "F15", {"entities" : qUnion([Q0]), "radius" : 2 * mm, "tangentPropagation" : true, "allowEdgeOverflow" : false});
        }
        {
            var Q0;
            {var subQ0=sQuery(id+"F0.wireOp",EDGE,"E22.filletArc");var subQ1=sQuery(id+"F0.wireOp",EDGE,"E7");var subQ2=sQuery(id+"F0.wireOp",EDGE,"E6");var subQ3=sQuery(id+"F0.wireOp",EDGE,"E5");var subQ4=sQuery(id+"F0.wireOp",EDGE,"E4");var subQ5=sQuery(id+"F0.wireOp",EDGE,"E1.bottom");var subQ6=sQuery(id+"F0.wireOp",EDGE,"E21.filletArc");var subQ7=sQuery(id+"F0.wireOp",EDGE,"E1.top");var subQ8=sQuery(id+"F0.wireOp",EDGE,"E1.left");var subQ9=sQuery(id+"F0.wireOp",EDGE,"E1.right");var subQ10=sQuery(id+"F0.wireOp",EDGE,"E23.filletArc");var subQ11=sQuery(id+"F0.wireOp",EDGE,"E24.filletArc");Q0=makeQuery(id+"F2.boolean.opBoolean","SPLIT",FACE,{"disambiguationData":[TD([makeQuery(id+"F1.opExtrude","SWEPT_FACE",FACE,{"disambiguationData":[OSD([subQ5])]})])],"derivedFrom":makeQuery(id+"F1.opExtrude","CAP_FACE",FACE,{"disambiguationData":[OSD([subQ5,subQ7,subQ8,subQ9,subQ4,subQ3,subQ2,subQ1,subQ6,subQ0,subQ10,subQ11])],"isStart":true})});}
            var sketch = newSketch(context, id + "F16", { "sketchPlane" : qUnion([Q0])});
            skLineSegment(sketch, "E79", {"start": v(0, 90) * mm, "end": v(0, 120) * mm, "construction": true});
            skArc(sketch, "E80", {"start": v(15, 120) * mm, "mid": v(0, 135) * mm, "end": v(-15, 120) * mm});
            skCircle(sketch, "E81", {"center": v(0, 120) * mm, "radius": 6 * mm});
            skLineSegment(sketch, "E82", {"start": v(-15, 120) * mm, "end": v(-15, 108) * mm});
            skLineSegment(sketch, "E83", {"start": v(15, 120) * mm, "end": v(15, 108) * mm});
            skLineSegment(sketch, "E84", {"start": v(-15, 108) * mm, "end": v(-33, 90) * mm});
            skLineSegment(sketch, "E85", {"start": v(15, 108) * mm, "end": v(33, 90) * mm});
            skLineSegment(sketch, "E86", {"start": v(-80, 0) * mm, "end": v(80, 0) * mm, "construction": true});
            skArc(sketch, "E87.MirrorCS", {"start": v(-15, 120) * mm, "mid": v(0, 135) * mm, "end": v(15, 120) * mm});
            skLineSegment(sketch, "E88.MirrorCS", {"start": v(80, 0) * mm, "end": v(-80, 0) * mm, "construction": true});
            skArc(sketch, "E89.MirrorCS", {"start": v(15, -120) * mm, "mid": v(0, -135) * mm, "end": v(-15, -120) * mm});
            skLineSegment(sketch, "E90.MirrorCS", {"start": v(-15, -108) * mm, "end": v(-33, -90) * mm});
            skCircle(sketch, "E91.MirrorC", {"center": v(0, -120) * mm, "radius": 6 * mm});
            skLineSegment(sketch, "E92.MirrorCS", {"start": v(-15, -120) * mm, "end": v(-15, -108) * mm});
            skLineSegment(sketch, "E93.MirrorCS", {"start": v(15, -120) * mm, "end": v(15, -108) * mm});
            skLineSegment(sketch, "E94.MirrorCS", {"start": v(15, -108) * mm, "end": v(33, -90) * mm});
            skLineSegment(sketch, "E95.MirrorCS", {"start": v(0, -90) * mm, "end": v(0, -120) * mm, "construction": true});
            skArc(sketch, "E96.MirrorCS", {"start": v(-15, -120) * mm, "mid": v(0, -135) * mm, "end": v(15, -120) * mm});
            skSolve(sketch);
        }
        {
            var Q0;
            {var subQ1=sQuery(id+"F16.wireOp",EDGE,"E94.MirrorCS");Q0=makeQuery(id+"F16.imprint","IMPRINT",FACE,{"disambiguationData":[TD([[makeQuery(id+"F16.imprint","IMPRINT",EDGE,{"derivedFrom":subQ1}),1.0]])]});}
            var Q1;
            Q1=makeQuery(id+"F16.imprint","IMPRINT",FACE,{"disambiguationData":[TD([[makeQuery(id+"F16.imprint","IMPRINT",EDGE,{"derivedFrom":sQuery(id+"F16.wireOp",EDGE,"E87.MirrorCS")}),-1.0]])]});
            var Q2;
            Q2=makeQuery(id+"F16.imprint","IMPRINT",FACE,{"disambiguationData":[TD([[makeQuery(id+"F16.imprint","IMPRINT",EDGE,{"derivedFrom":makeQuery(id+"F1.opExtrude","CAP_EDGE",EDGE,{"disambiguationData":[OSD([sQuery(id+"F0.wireOp",EDGE,"E1.left")])],"isStart":true})}),-1.0]])]});
            var Q3;
            Q3=makeQuery(id+"F2.opExtrude","CAP_FACE",FACE,{"disambiguationData":[OSD([sQuery(id+"F0.wireOp",EDGE,"E12"),sQuery(id+"F0.wireOp",EDGE,"E13"),sQuery(id+"F0.wireOp",EDGE,"E14"),sQuery(id+"F0.wireOp",EDGE,"E15"),sQuery(id+"F0.wireOp",EDGE,"E17.filletArc"),sQuery(id+"F0.wireOp",EDGE,"E18.filletArc"),sQuery(id+"F0.wireOp",EDGE,"E19.filletArc"),sQuery(id+"F0.wireOp",EDGE,"E20.filletArc"),sQuery(id+"F0.wireOp",EDGE,"E25.0"),sQuery(id+"F0.wireOp",EDGE,"E25.1"),sQuery(id+"F0.wireOp",EDGE,"E25.2"),sQuery(id+"F0.wireOp",EDGE,"E25.3"),sQuery(id+"F0.wireOp",EDGE,"E25.4"),sQuery(id+"F0.wireOp",EDGE,"E25.5"),sQuery(id+"F0.wireOp",EDGE,"E25.6"),sQuery(id+"F0.wireOp",EDGE,"E25.7")])],"isStart":false});
            extrude(context, id + "F17", {"entities" : qUnion([Q0, Q1, Q2]), "endBound" : BoundingType.UP_TO_SURFACE, "endBoundEntityFace" : qUnion([Q3]), "depth" : 25 * mm});
        }
    });
